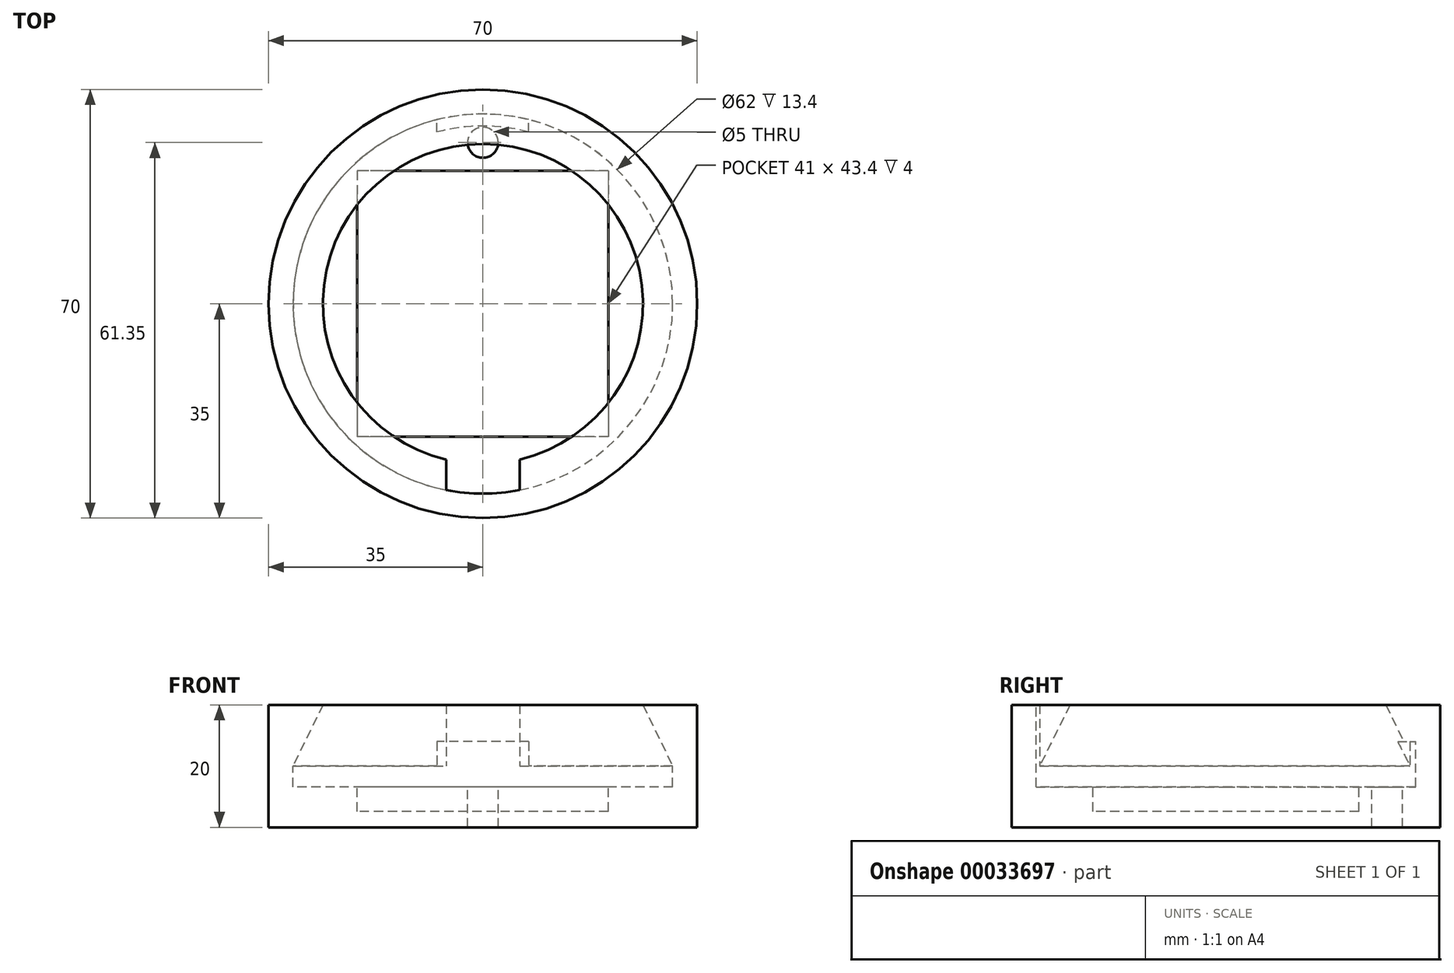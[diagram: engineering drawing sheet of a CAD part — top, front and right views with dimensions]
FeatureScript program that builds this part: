
annotation { "Feature Type Name" : "Feature", "Feature Type Description" : "" }
export const myFeature = defineFeature(function(context is Context, id is Id, definition is map)
    precondition{}
    {
        {
            var Q0;
            Q0=qCreatedBy(makeId("Top.planeOp"),FACE);
            var sketch = newSketch(context, id + "F0", { "sketchPlane" : qUnion([Q0])});
            skCircle(sketch, "E0", {"center": v(0, 0) * mm, "radius": 35 * mm});
            skSolve(sketch);
        }
        {
            var Q0;
            Q0=makeQuery(id+"F0.imprint","IMPRINT",FACE,{"disambiguationData":[TD([[makeQuery(id+"F0.imprint","IMPRINT",EDGE,{"derivedFrom":sQuery(id+"F0.wireOp",EDGE,"E0")}),1.0]])]});
            extrude(context, id + "F1", {"entities" : qUnion([Q0]), "depth" : 10 * mm});
        }
        {
            var Q0;
            Q0=makeQuery(id+"F1.opExtrude","CAP_FACE",FACE,{"disambiguationData":[OSD([sQuery(id+"F0.wireOp",EDGE,"E0")])],"isStart":false});
            var sketch = newSketch(context, id + "F2", { "sketchPlane" : qUnion([Q0])});
            skCircle(sketch, "E1", {"center": v(0, 0) * mm, "radius": 31 * mm});
            skLineSegment(sketch, "E2.rect.bottom", {"start": v(20.5, 21.7) * mm, "end": v(-20.5, 21.7) * mm});
            skLineSegment(sketch, "E2.rect.top", {"start": v(20.5, -21.7) * mm, "end": v(-20.5, -21.7) * mm});
            skLineSegment(sketch, "E2.rect.left", {"start": v(20.5, 21.7) * mm, "end": v(20.5, -21.7) * mm});
            skLineSegment(sketch, "E2.rect.right", {"start": v(-20.5, 21.7) * mm, "end": v(-20.5, -21.7) * mm});
            skCircle(sketch, "E3", {"center": v(0, 26.35) * mm, "radius": 2.5 * mm});
            skLineSegment(sketch, "E4", {"start": v(0, 21.7) * mm, "end": v(0, 31) * mm, "construction": true});
            skLineSegment(sketch, "E5", {"start": v(-7.5, 20.08) * mm, "end": v(0, 20.08) * mm});
            skLineSegment(sketch, "E6", {"start": v(0, 20.08) * mm, "end": v(7.5, 20.08) * mm});
            skLineSegment(sketch, "E7", {"start": v(7.5, 20.08) * mm, "end": v(7.5, 30.08) * mm});
            skLineSegment(sketch, "E8", {"start": v(-7.5, 20.08) * mm, "end": v(-7.5, 30.08) * mm});
            skLineSegment(sketch, "E9", {"start": v(0, -20.41) * mm, "end": v(6, -20.41) * mm});
            skLineSegment(sketch, "E10", {"start": v(6, -20.41) * mm, "end": v(6, -30.41) * mm});
            skLineSegment(sketch, "E11", {"start": v(0, -20.41) * mm, "end": v(-6, -20.41) * mm});
            skLineSegment(sketch, "E12", {"start": v(-6, -20.41) * mm, "end": v(-6, -30.41) * mm});
            skLineSegment(sketch, "E13", {"start": v(-6.35, 21.7) * mm, "end": v(-6.35, 28.85) * mm, "construction": true});
            skLineSegment(sketch, "E14", {"start": v(-6.35, 28.85) * mm, "end": v(0, 28.85) * mm, "construction": true});
            skSolve(sketch);
        }
        {
            var Q0;
            Q0=makeQuery(id+"F2.imprint","IMPRINT",FACE,{"disambiguationData":[TD([[makeQuery(id+"F2.imprint","IMPRINT",EDGE,{"derivedFrom":sQuery(id+"F2.wireOp",EDGE,"E1")}),1.0]])]});
            var Q1;
            {var subQ9=sQuery(id+"F2.wireOp",EDGE,"E2.rect.right");Q1=makeQuery(id+"F2.imprint","IMPRINT",FACE,{"disambiguationData":[TD([[makeQuery(id+"F2.imprint","IMPRINT",EDGE,{"derivedFrom":subQ9}),-1.0]])]});}
            var Q2;
            {var subQ9=sQuery(id+"F2.wireOp",EDGE,"E2.rect.left");Q2=makeQuery(id+"F2.imprint","IMPRINT",FACE,{"disambiguationData":[TD([[makeQuery(id+"F2.imprint","IMPRINT",EDGE,{"derivedFrom":subQ9}),1.0]])]});}
            var Q3;
            Q3=makeQuery(id+"F2.imprint","IMPRINT",FACE,{"disambiguationData":[TD([[makeQuery(id+"F2.imprint","IMPRINT",EDGE,{"derivedFrom":sQuery(id+"F2.wireOp",EDGE,"E3")}),-1.0]])]});
            extrude(context, id + "F3", {"entities" : qUnion([Q0, Q1, Q2, Q3]), "operationType" : NewBodyOperationType.REMOVE, "oppositeDirection" : true, "depth" : 3.4 * mm});
        }
        {
            var Q0;
            Q0=makeQuery(id+"F2.imprint","IMPRINT",FACE,{"disambiguationData":[TD([[makeQuery(id+"F2.imprint","IMPRINT",EDGE,{"derivedFrom":sQuery(id+"F2.wireOp",EDGE,"E3")}),1.0]])]});
            extrude(context, id + "F4", {"entities" : qUnion([Q0]), "operationType" : NewBodyOperationType.REMOVE, "endBound" : BoundingType.THROUGH_ALL, "oppositeDirection" : true, "depth" : 25 * mm});
        }
        {
            var Q0;
            Q0=makeQuery(id+"F2.imprint","IMPRINT",FACE,{"disambiguationData":[TD([[makeQuery(id+"F2.imprint","IMPRINT",EDGE,{"derivedFrom":sQuery(id+"F2.wireOp",EDGE,"E2.rect.bottom")}),1.0]])]});
            var Q1;
            {var subQ3=sQuery(id+"F2.wireOp",EDGE,"E5");Q1=makeQuery(id+"F2.imprint","IMPRINT",FACE,{"disambiguationData":[TD([[makeQuery(id+"F2.imprint","IMPRINT",EDGE,{"derivedFrom":subQ3}),1.0]])]});}
            var Q2;
            {var subQ6=sQuery(id+"F2.wireOp",EDGE,"E9");Q2=makeQuery(id+"F2.imprint","IMPRINT",FACE,{"disambiguationData":[TD([[makeQuery(id+"F2.imprint","IMPRINT",EDGE,{"derivedFrom":subQ6}),-1.0]])]});}
            var Q3;
            Q3=makeQuery(id+"F2.imprint","IMPRINT",FACE,{"disambiguationData":[TD([[makeQuery(id+"F2.imprint","IMPRINT",EDGE,{"derivedFrom":sQuery(id+"F2.wireOp",EDGE,"09bc0f0c-9f7c-4021-b2c2-f7e8885750cd.rect.bottom")}),-1.0]])]});
            extrude(context, id + "F5", {"entities" : qUnion([Q0, Q1, Q2, Q3]), "operationType" : NewBodyOperationType.REMOVE, "oppositeDirection" : true, "depth" : (3.4 + 4) * mm});
        }
        {
            var Q0;
            Q0=makeQuery(id+"F2.imprint","IMPRINT",FACE,{"disambiguationData":[TD([[makeQuery(id+"F2.imprint","IMPRINT",EDGE,{"derivedFrom":sQuery(id+"F2.wireOp",EDGE,"E1")}),-1.0]])]});
            extrude(context, id + "F6", {"entities" : qUnion([Q0]), "operationType" : NewBodyOperationType.ADD, "depth" : 10 * mm, "hasDraft" : true, "draftAngle" : 26 * degree});
        }
        {
            var Q0;
            Q0=makeQuery(id+"F6.opExtrude","CAP_FACE",FACE,{"disambiguationData":[OSD([sQuery(id+"F0.wireOp",EDGE,"E0"),sQuery(id+"F2.wireOp",EDGE,"E1")])],"isStart":false});
            var sketch = newSketch(context, id + "F7", { "sketchPlane" : qUnion([Q0])});
            skCircle(sketch, "E15", {"center": v(0, 0) * mm, "radius": 35 * mm});
            skSolve(sketch);
        }
        {
            var Q0;
            Q0=makeQuery(id+"F7.imprint","IMPRINT",FACE,{"disambiguationData":[TD([[makeQuery(id+"F7.imprint","IMPRINT",EDGE,{"derivedFrom":sQuery(id+"F7.wireOp",EDGE,"E15")}),-1.0]])]});
            extrude(context, id + "F8", {"entities" : qUnion([Q0]), "operationType" : NewBodyOperationType.REMOVE, "endBound" : BoundingType.THROUGH_ALL, "oppositeDirection" : true, "depth" : 25 * mm});
        }
        {
            var Q0;
            Q0=makeQuery(id+"F2.imprint","IMPRINT",FACE,{"disambiguationData":[TD([[makeQuery(id+"F2.imprint","IMPRINT",EDGE,{"derivedFrom":sQuery(id+"F2.wireOp",EDGE,"E3")}),-1.0]])]});
            var Q1;
            {var subQ3=sQuery(id+"F2.wireOp",EDGE,"E5");Q1=makeQuery(id+"F2.imprint","IMPRINT",FACE,{"disambiguationData":[TD([[makeQuery(id+"F2.imprint","IMPRINT",EDGE,{"derivedFrom":subQ3}),1.0]])]});}
            var Q2;
            Q2=makeQuery(id+"F2.imprint","IMPRINT",FACE,{"disambiguationData":[TD([[makeQuery(id+"F2.imprint","IMPRINT",EDGE,{"derivedFrom":sQuery(id+"F2.wireOp",EDGE,"E3")}),1.0]])]});
            extrude(context, id + "F9", {"entities" : qUnion([Q0, Q1, Q2]), "operationType" : NewBodyOperationType.REMOVE, "depth" : 4 * mm});
        }
        {
            var Q0;
            {var subQ3=sQuery(id+"F2.wireOp",EDGE,"E1");var subQ5=sQuery(id+"F2.wireOp",EDGE,"E10");var subQ7=makeQuery(id+"F2.imprint","INTERSECT",VERTEX,{"derivedFrom":[subQ3,subQ5]});Q0=makeQuery(id+"F2.imprint","IMPRINT",FACE,{"disambiguationData":[TD([[makeQuery(id+"F2.imprint","IMPRINT",EDGE,{"disambiguationData":[TD([[subQ7,1.0]])],"derivedFrom":subQ3}),1.0]])]});}
            var Q1;
            {var subQ6=sQuery(id+"F2.wireOp",EDGE,"E9");Q1=makeQuery(id+"F2.imprint","IMPRINT",FACE,{"disambiguationData":[TD([[makeQuery(id+"F2.imprint","IMPRINT",EDGE,{"derivedFrom":subQ6}),-1.0]])]});}
            extrude(context, id + "F10", {"entities" : qUnion([Q0, Q1]), "operationType" : NewBodyOperationType.REMOVE, "endBound" : BoundingType.THROUGH_ALL, "depth" : 25 * mm});
        }
    });
